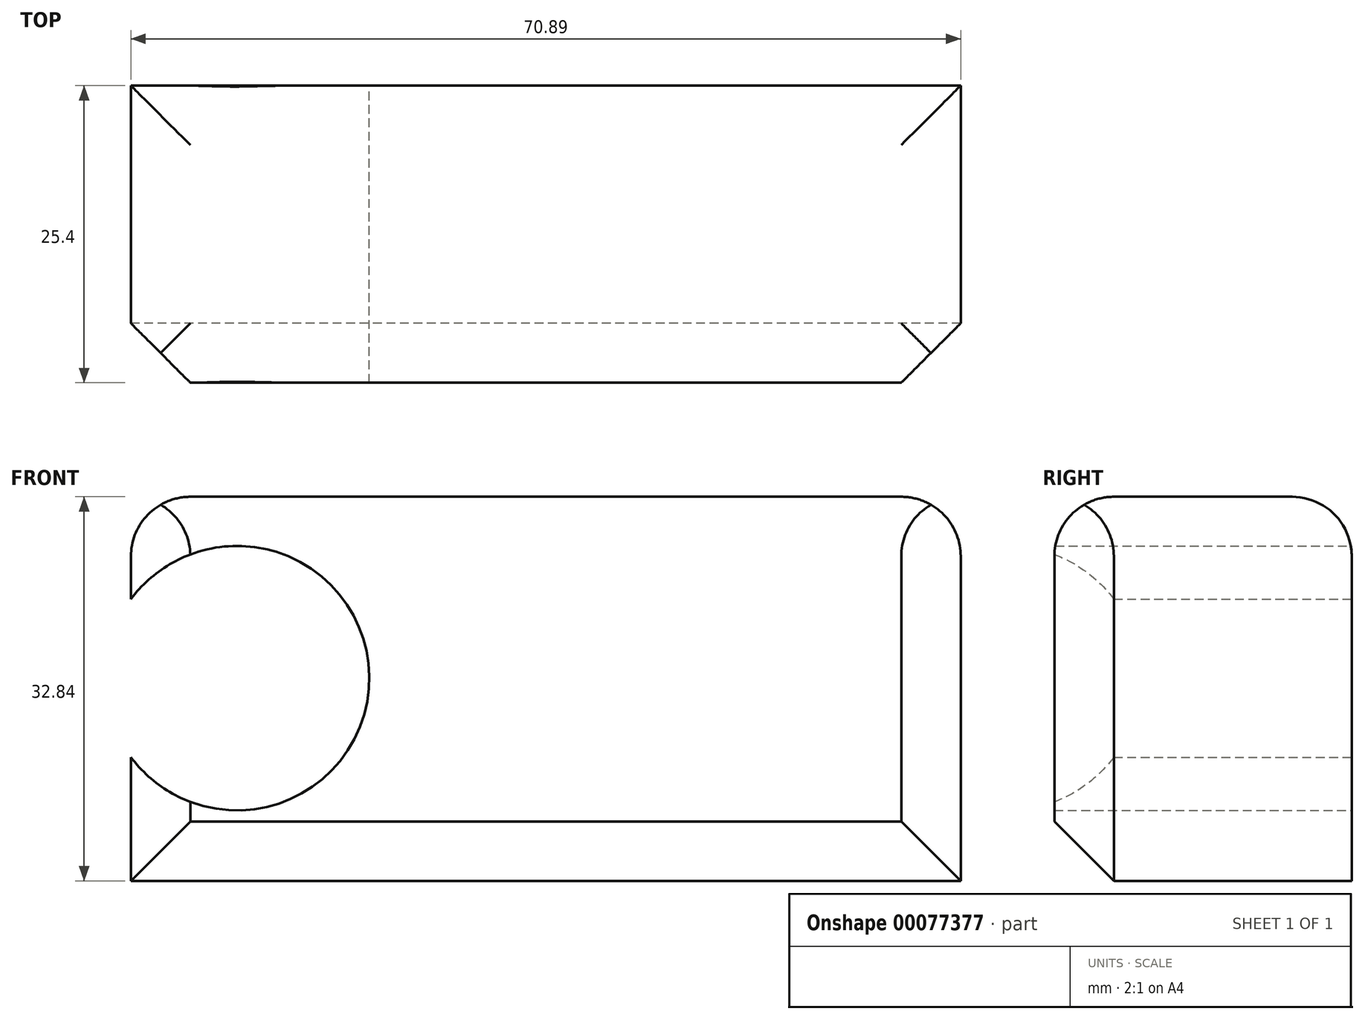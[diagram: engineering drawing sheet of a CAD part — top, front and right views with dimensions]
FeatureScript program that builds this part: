
annotation { "Feature Type Name" : "Feature", "Feature Type Description" : "" }
export const myFeature = defineFeature(function(context is Context, id is Id, definition is map)
    precondition{}
    {
        {
            var Q0;
            Q0=qCreatedBy(makeId("Front.planeOp"),FACE);
            var sketch = newSketch(context, id + "F0", { "sketchPlane" : qUnion([Q0])});
            skLineSegment(sketch, "E0.bottom", {"start": v(-46.37, 25.26) * mm, "end": v(24.52, 25.26) * mm});
            skLineSegment(sketch, "E0.top", {"start": v(-46.37, -7.58) * mm, "end": v(24.52, -7.58) * mm});
            skLineSegment(sketch, "E0.left", {"start": v(-46.37, 25.26) * mm, "end": v(-46.37, -7.58) * mm});
            skLineSegment(sketch, "E0.right", {"start": v(24.52, 25.26) * mm, "end": v(24.52, -7.58) * mm});
            skCircle(sketch, "E1", {"center": v(-37.31, 9.75) * mm, "radius": 11.3 * mm});
            skSolve(sketch);
        }
        {
            var Q0;
            {var subQ0=sQuery(id+"F0.wireOp",EDGE,"E1");var subQ1=sQuery(id+"F0.wireOp",EDGE,"E0.left");var subQ2=makeQuery(id+"F0.imprint","INTERSECT",VERTEX,{"disambiguationData":[OD(0.0)],"derivedFrom":[subQ1,subQ0]});Q0=makeQuery(id+"F0.imprint","IMPRINT",FACE,{"disambiguationData":[TD([[makeQuery(id+"F0.imprint","IMPRINT",EDGE,{"disambiguationData":[TD([[subQ2,-1.0]])],"derivedFrom":subQ1}),1.0]])]});}
            var Q1;
            {var subQ4=sQuery(id+"F0.wireOp",EDGE,"E0.bottom");Q1=makeQuery(id+"F0.imprint","IMPRINT",FACE,{"disambiguationData":[TD([[makeQuery(id+"F0.imprint","IMPRINT",EDGE,{"derivedFrom":subQ4}),-1.0]])]});}
            extrude(context, id + "F1", {"entities" : qUnion([Q0, Q1]), "depth" : 25.4 * mm});
        }
        {
            var Q0;
            Q0=makeQuery(id+"F1.opExtrude","SWEPT_FACE",FACE,{"disambiguationData":[OSD([sQuery(id+"F0.wireOp",EDGE,"E0.bottom")])]});
            var Q1;
            Q1=makeQuery(id+"F1.opExtrude","CAP_EDGE",EDGE,{"disambiguationData":[OSD([sQuery(id+"F0.wireOp",EDGE,"E0.bottom")])],"isStart":false});
            fillet(context, id + "F2", {"entities" : qUnion([Q0, Q1]), "radius" : 5.08 * mm, "tangentPropagation" : true, "allowEdgeOverflow" : false});
        }
        {
            var Q0;
            Q0=makeQuery(id+"F1.opExtrude","CAP_EDGE",EDGE,{"disambiguationData":[OSD([sQuery(id+"F0.wireOp",EDGE,"E0.left")])],"isStart":false});
            var Q1;
            Q1=makeQuery(id+"F1.opExtrude","CAP_EDGE",EDGE,{"disambiguationData":[OSD([sQuery(id+"F0.wireOp",EDGE,"E0.top")])],"isStart":false});
            var Q2;
            Q2=makeQuery(id+"F1.opExtrude","CAP_EDGE",EDGE,{"disambiguationData":[OSD([sQuery(id+"F0.wireOp",EDGE,"E0.right")])],"isStart":false});
            var Q3;
            {var subQ0=sQuery(id+"F0.wireOp",EDGE,"E0.bottom");Q3=makeQuery(id+"F2.opFillet","BLEND_EDGE",EDGE,{"blendedFrom":[makeQuery(id+"F1.opExtrude","CAP_EDGE",EDGE,{"disambiguationData":[OSD([subQ0])],"isStart":false}),makeQuery(id+"F1.opExtrude","CAP_FACE",FACE,{"disambiguationData":[OSD([subQ0,sQuery(id+"F0.wireOp",EDGE,"E0.top"),sQuery(id+"F0.wireOp",EDGE,"E0.left"),sQuery(id+"F0.wireOp",EDGE,"E0.right")])],"isStart":false})],"blendedInto":[makeQuery(id+"F1.opExtrude","CAP_FACE",FACE,{"disambiguationData":[OSD([subQ0,sQuery(id+"F0.wireOp",EDGE,"E0.top"),sQuery(id+"F0.wireOp",EDGE,"E0.left"),sQuery(id+"F0.wireOp",EDGE,"E0.right")])],"isStart":false})]});}
            chamfer(context, id + "F3", {"entities" : qUnion([Q0, Q1, Q2, Q3]), "width" : 5.08 * mm, "tangentPropagation" : true});
        }
    });
